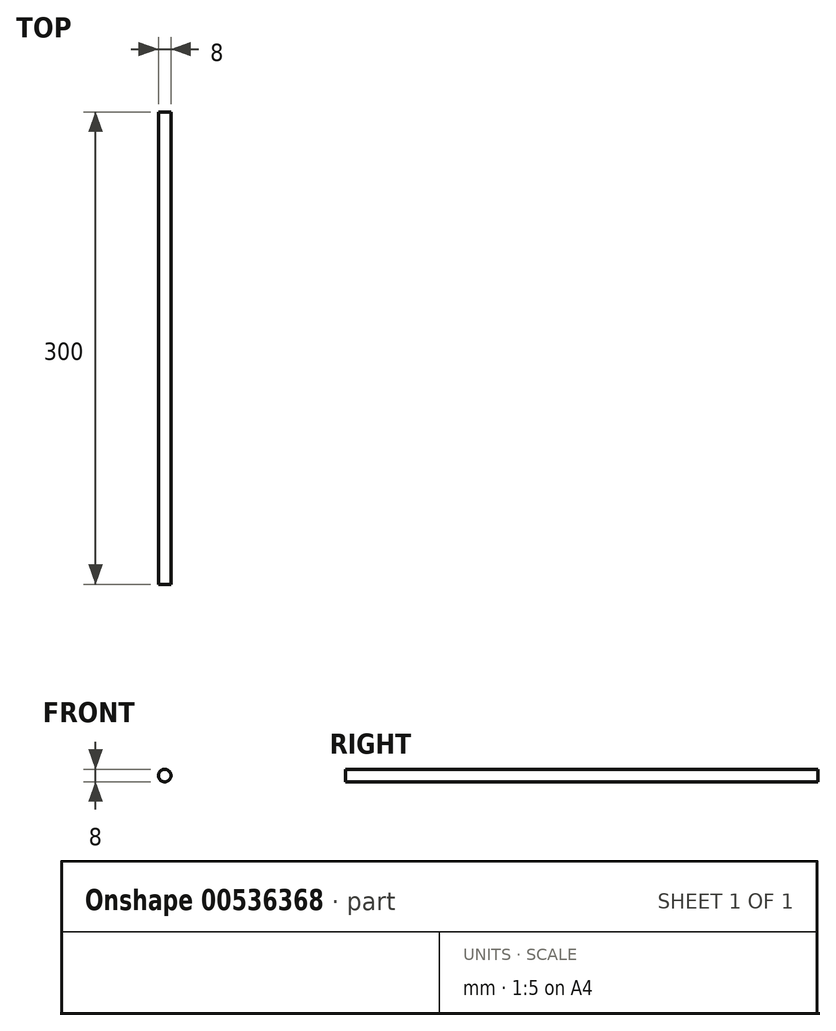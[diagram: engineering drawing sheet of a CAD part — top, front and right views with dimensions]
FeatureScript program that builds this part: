
annotation { "Feature Type Name" : "Feature", "Feature Type Description" : "" }
export const myFeature = defineFeature(function(context is Context, id is Id, definition is map)
    precondition{}
    {
        {
            var Q0;
            Q0=qCreatedBy(makeId("Front.planeOp"),FACE);
            var sketch = newSketch(context, id + "F0", { "sketchPlane" : qUnion([Q0])});
            skCircle(sketch, "E0", {"center": v(0, 0) * mm, "radius": 4 * mm});
            skSolve(sketch);
        }
        {
            var Q0;
            Q0=makeQuery(id+"F0.imprint","IMPRINT",FACE,{"disambiguationData":[TD([[makeQuery(id+"F0.imprint","IMPRINT",EDGE,{"derivedFrom":sQuery(id+"F0.wireOp",EDGE,"E0")}),1.0]])]});
            extrude(context, id + "F1", {"entities" : qUnion([Q0]), "depth" : 300 * mm, "offsetDistance" : 25 * mm});
        }
    });
